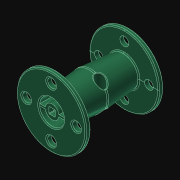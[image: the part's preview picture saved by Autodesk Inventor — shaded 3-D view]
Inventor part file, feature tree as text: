
AUTODESK INVENTOR PART (.ipt)
format: ipt  version: 2021.3 (Build 253353010, 353A)  size: 1,070,080 bytes
history: native  units: in
note: dims shown in document units (in); Inventor stores cm internally (conversion verified against a paired STEP export)
features: mirror x1, imported_body x1
ambient origin geometry x8: Origin, YZ Plane, XZ Plane, XY Plane, X Axis, Y Axis, Z Axis, Center Point
bodies: Body1 (feature_tree)
feature tree (2):
  mirror  "Mirror1"
  imported_body  "Base1"
